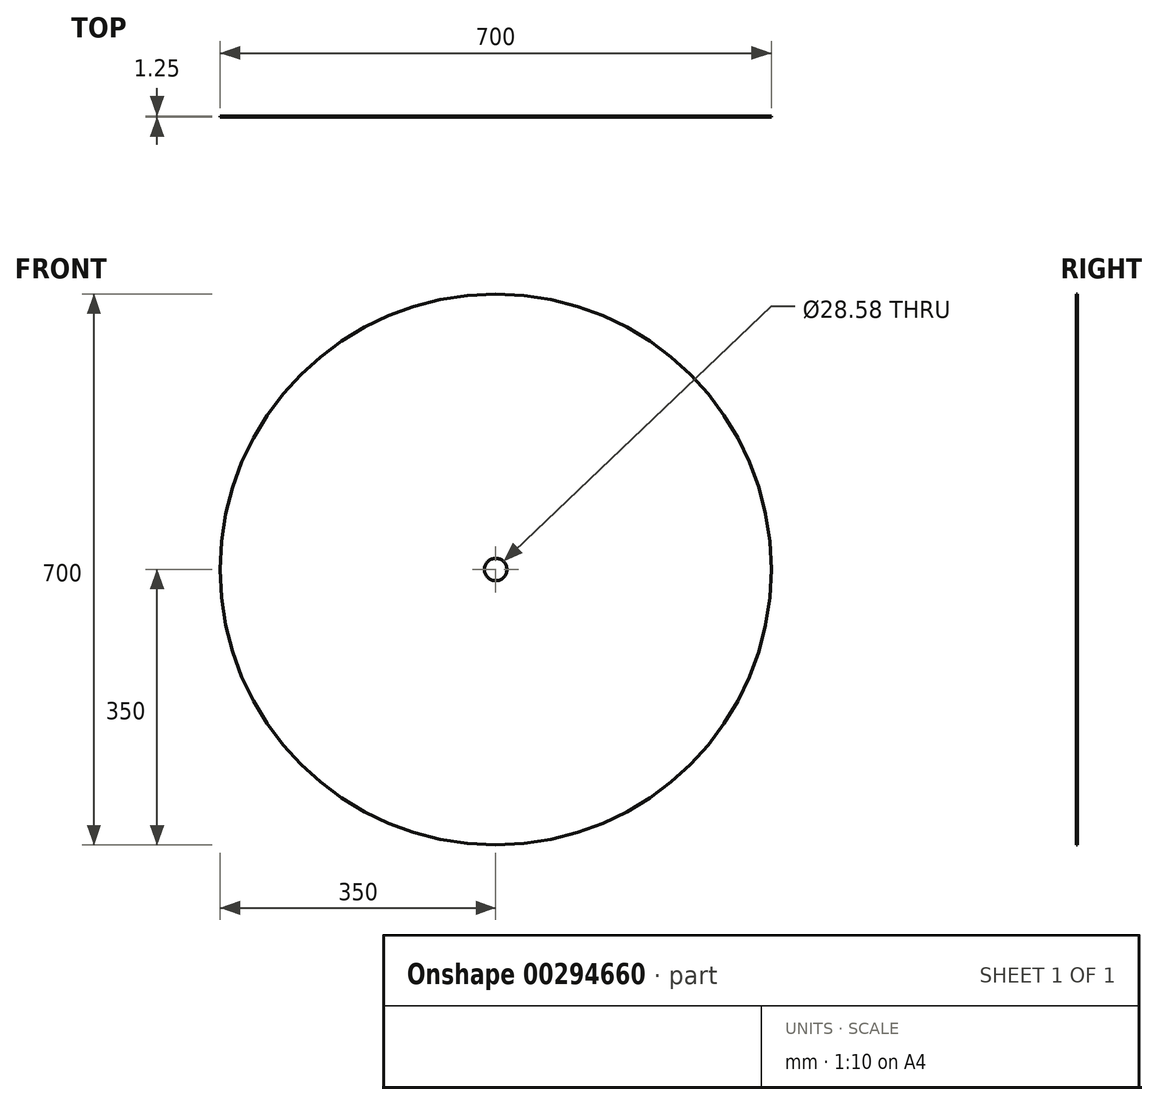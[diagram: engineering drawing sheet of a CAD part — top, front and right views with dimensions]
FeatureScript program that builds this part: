
annotation { "Feature Type Name" : "Feature", "Feature Type Description" : "" }
export const myFeature = defineFeature(function(context is Context, id is Id, definition is map)
    precondition{}
    {
        {
            var Q0;
            Q0=qCreatedBy(makeId("Front.planeOp"),FACE);
            var sketch = newSketch(context, id + "F0", { "sketchPlane" : qUnion([Q0])});
            skCircle(sketch, "E0", {"center": v(0, 0) * mm, "radius": 350 * mm});
            skSolve(sketch);
        }
        {
            var Q0;
            Q0=makeQuery(id+"F0.imprint","IMPRINT",FACE,{"disambiguationData":[TD([[makeQuery(id+"F0.imprint","IMPRINT",EDGE,{"derivedFrom":sQuery(id+"F0.wireOp",EDGE,"E0")}),1.0]])]});
            extrude(context, id + "F1", {"entities" : qUnion([Q0]), "depth" : 1.25 * mm});
        }
        {
            var Q0;
            Q0=makeQuery(id+"F1.opExtrude","CAP_FACE",FACE,{"disambiguationData":[OSD([sQuery(id+"F0.wireOp",EDGE,"E0")])],"isStart":true});
            var sketch = newSketch(context, id + "F2", { "sketchPlane" : qUnion([Q0])});
            skCircle(sketch, "E1", {"center": v(0, 0) * mm, "radius": 14.29 * mm});
            skSolve(sketch);
        }
        {
            var Q0;
            Q0 = qSketchRegion(id + "F2", true);
            extrude(context, id + "F3", {"entities" : qUnion([Q0]), "operationType" : NewBodyOperationType.REMOVE, "oppositeDirection" : true, "depth" : 10 * mm});
        }
    });
